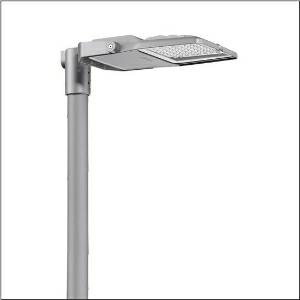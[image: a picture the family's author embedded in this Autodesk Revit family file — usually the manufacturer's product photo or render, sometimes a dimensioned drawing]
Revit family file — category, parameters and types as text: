
# Revit family: floodlight_fl_21_iq_mini___pl64_5xa7771d2e3a_d262
name_source: partatom
category: Lighting Fixtures
units: mm (PartAtom-declared; Revit-internal decimal feet)

## family parameters
Cut with Voids When Loaded = No
Host = Face
Light Source = No
Part Type = Normal
Room Calculation Point = No
Round Connector Dimension = Use Diameter
Shared = No

## types (1)
- --- (1 x LED, 17220 lm, 143 W, 3000K)
    Apparent Load = 143 VA
    CIE Flux Codes = 28 80 98 100 100
    Color Rendering = 70
    Color Temperature = 3000K
    Default Elevation = 1800 mm
    Description = Floodlight FL 21 iQ mini, floodlight, primary light control with lens, of PMMA, primary optical cover: protective disc, of toughened safety glass, transparent, light distribution: PL64, light emission: direct distribution, installation type: surface-mounted, LED, High Power LED, rated luminous flux: 17.220lm, luminous efficacy: 120lm/W, light colour: 730, colour temperature: 3000K, control gear: iQ Comfort/DALI, control: Auto-Match, Temp-Guard, Lumen-Switch, Night-Set, Smart-Wire, Light-Fading, Desk-Remote (wireless, voltage-free reading and setting of iQ features in the workshop via application-optimized NFC function/RFID function), optimised constant luminous flux control (CLO 2.0), with terminal, 6-pole, mains connection: 220..240V, AC, 50/60Hz, start of lifetime: 143W, end of service life: 152W, reduction: 61W, luminaire housing, of diecast aluminium, powder-coated, Siteco® metallic grey (DB 702S), corrosivity category C5 mid according to DIN EN ISO 12944, suitable for swimming pools, chlorine-resistant, sealing non-destructively replaceable, please order mast flange separately, mast bracket, of steel, galvanised, powder-coated, Siteco® metallic grey (DB 702S), protection rating (complete): IP66, insulation class (complete): insulation class II (safety insulation), certification: CE, ENEC, VDE, protection symbol: D, impact resistance: IK08, permissible operating ambient temperature: -40..+40°C, permissible operating ambient temperature for outdoor applications: -40..+50°C, standard: DIN EN 12944, LABS conformity tested according to VDMA 24364:2018-05, packaging unit: 1 piece

Light Distribution: PL64
    Height = 70 mm
    Lamp = 1 x LED
    Lamp Light Flux = 17220 lm
    Lamp Power = 143 W
    Lamp count = 1
    Length = 485 mm
    Luminous efficacy = 120 lm/W
    Manufacturer = Siteco
    ModVariant = No
    Model = 5XA7771D2E3A
    Number of Poles = 1
    OnlyDefault = Yes
    Power Factor = 1
    Product Name = Floodlight FL 21 iQ mini | PL64
    Product group = floodlight | pylon annexe
    ProductGroupID = 6201
    Protection Class = Protection class II
    Protection Degree = IP 66
    RLX_Detail_Level = 1
    RLX_Emergency_Light_Flux = 0 lm
    RLX_Emergency_Type = 0
    RLX_Emergency_Type_DB = No
    RlxData = <blob elided: 101529 chars, md5=25598f8d>
    Socket = socket
    Standby Power = 0 W
    System Light Flux = 17220 lm
    System Power = 143 W
    Type Comments = factory setting: luminous flux: 100 % | dim-lin: 254 | 730 mA
    Type Image = l_1007125.jpg
    URL = http://relux.com
    VarID = @adj_187533
    Voltage = 0 V
    Weight = 0.00 kg
    Width = 337 mm

## geometry (parser evidence)
native form markers: Blend x4, Sweep x12
no freeform markers — native parametric forms only
